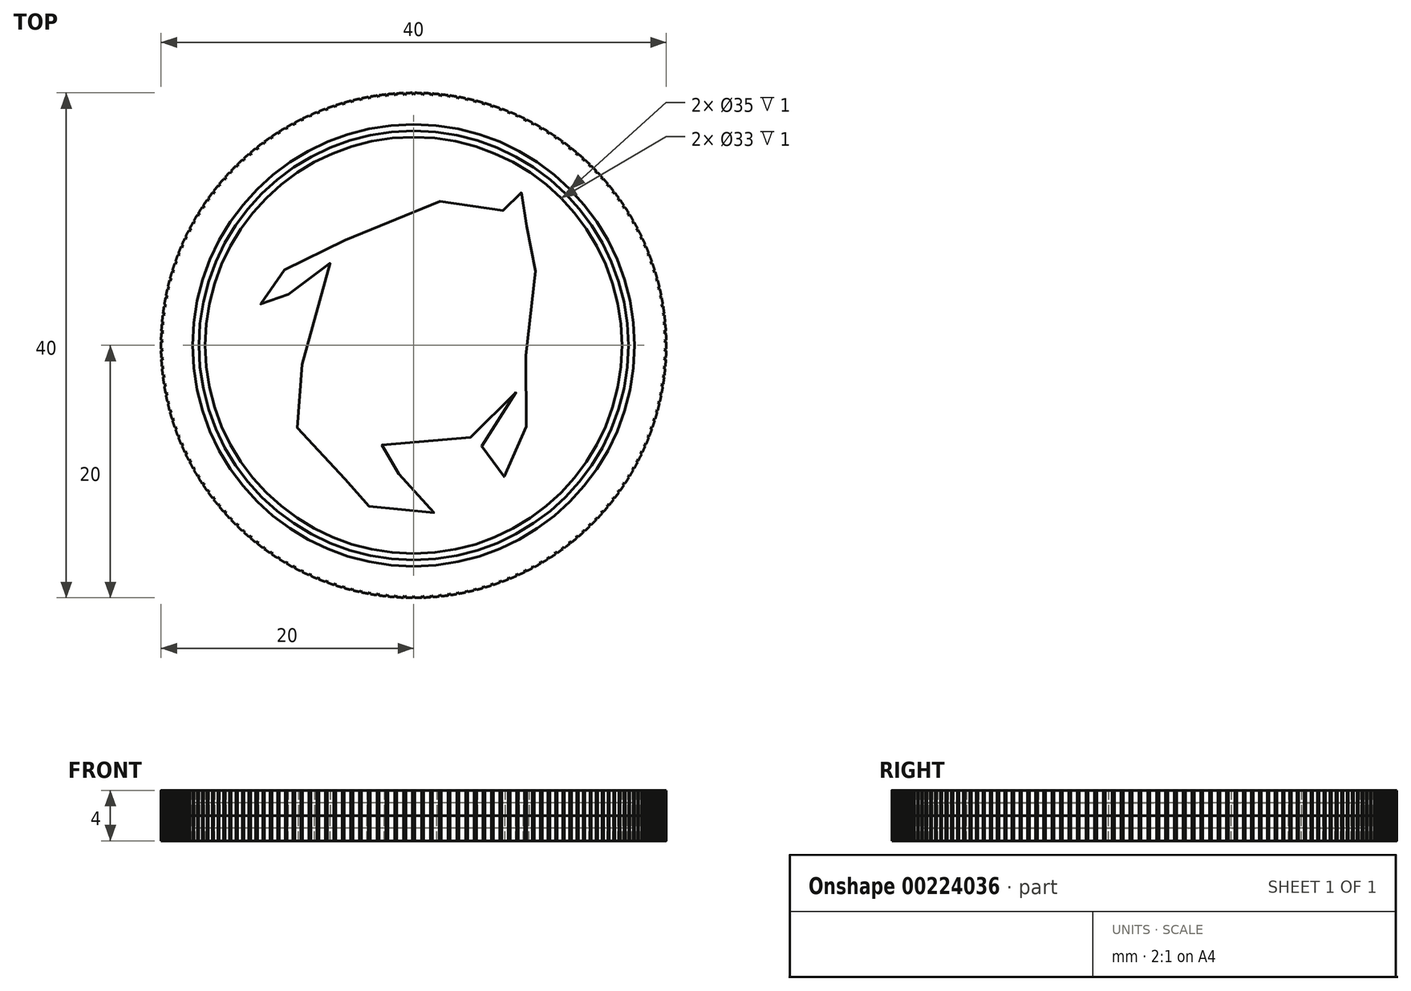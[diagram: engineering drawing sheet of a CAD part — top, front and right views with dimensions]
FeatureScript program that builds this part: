
annotation { "Feature Type Name" : "Feature", "Feature Type Description" : "" }
export const myFeature = defineFeature(function(context is Context, id is Id, definition is map)
    precondition{}
    {
        {
            var Q0;
            Q0=qCreatedBy(makeId("Top.planeOp"),FACE);
            var sketch = newSketch(context, id + "F0", { "sketchPlane" : qUnion([Q0])});
            skCircle(sketch, "E0", {"center": v(0, 0) * mm, "radius": 20 * mm});
            skCircle(sketch, "E1", {"center": v(0, 0) * mm, "radius": 17.5 * mm});
            skCircle(sketch, "E2", {"center": v(0, 0) * mm, "radius": 17 * mm});
            skCircle(sketch, "E3", {"center": v(0, 0) * mm, "radius": 16.5 * mm});
            skLineSegment(sketch, "E4", {"start": v(0, 19.85) * mm, "end": v(0.09, 20) * mm});
            skLineSegment(sketch, "E5", {"start": v(0, 19.85) * mm, "end": v(-0.09, 20) * mm});
            skPoint(sketch, "E6.center", {"position": v(0.03, 0) * mm});
            skLineSegment(sketch, "E7.1.0", {"start": v(0.7, 19.84) * mm, "end": v(0.8, 19.98) * mm});
            skLineSegment(sketch, "E7.1.1", {"start": v(0.7, 19.84) * mm, "end": v(0.62, 20) * mm});
            skLineSegment(sketch, "E7.2.0", {"start": v(1.4, 19.8) * mm, "end": v(1.5, 19.94) * mm});
            skLineSegment(sketch, "E7.2.1", {"start": v(1.4, 19.8) * mm, "end": v(1.32, 19.96) * mm});
            skLineSegment(sketch, "E7.3.0", {"start": v(2.1, 19.74) * mm, "end": v(2.2, 19.88) * mm});
            skLineSegment(sketch, "E7.3.1", {"start": v(2.1, 19.74) * mm, "end": v(2.03, 19.9) * mm});
            skLineSegment(sketch, "E7.4.0", {"start": v(2.8, 19.65) * mm, "end": v(2.9, 19.79) * mm});
            skLineSegment(sketch, "E7.4.1", {"start": v(2.8, 19.65) * mm, "end": v(2.73, 19.81) * mm});
            skLineSegment(sketch, "E7.5.0", {"start": v(3.49, 19.54) * mm, "end": v(3.6, 19.67) * mm});
            skLineSegment(sketch, "E7.5.1", {"start": v(3.49, 19.54) * mm, "end": v(3.43, 19.7) * mm});
            skLineSegment(sketch, "E7.6.0", {"start": v(4.17, 19.4) * mm, "end": v(4.29, 19.53) * mm});
            skLineSegment(sketch, "E7.6.1", {"start": v(4.17, 19.4) * mm, "end": v(4.12, 19.57) * mm});
            skLineSegment(sketch, "E7.7.0", {"start": v(4.86, 19.25) * mm, "end": v(4.98, 19.37) * mm});
            skLineSegment(sketch, "E7.7.1", {"start": v(4.86, 19.25) * mm, "end": v(4.8, 19.41) * mm});
            skLineSegment(sketch, "E7.8.0", {"start": v(5.53, 19.06) * mm, "end": v(5.66, 19.18) * mm});
            skLineSegment(sketch, "E7.8.1", {"start": v(5.53, 19.06) * mm, "end": v(5.49, 19.23) * mm});
            skLineSegment(sketch, "E7.9.0", {"start": v(6.2, 18.86) * mm, "end": v(6.33, 18.97) * mm});
            skLineSegment(sketch, "E7.9.1", {"start": v(6.2, 18.86) * mm, "end": v(6.17, 19.03) * mm});
            skLineSegment(sketch, "E7.10.0", {"start": v(6.86, 18.63) * mm, "end": v(7, 18.74) * mm});
            skLineSegment(sketch, "E7.10.1", {"start": v(6.86, 18.63) * mm, "end": v(6.83, 18.8) * mm});
            skLineSegment(sketch, "E7.11.0", {"start": v(7.52, 18.37) * mm, "end": v(7.65, 18.48) * mm});
            skLineSegment(sketch, "E7.11.1", {"start": v(7.52, 18.37) * mm, "end": v(7.5, 18.54) * mm});
            skLineSegment(sketch, "E7.12.0", {"start": v(8.16, 18.1) * mm, "end": v(8.3, 18.2) * mm});
            skLineSegment(sketch, "E7.12.1", {"start": v(8.16, 18.1) * mm, "end": v(8.14, 18.27) * mm});
            skLineSegment(sketch, "E7.13.0", {"start": v(8.8, 17.8) * mm, "end": v(8.94, 17.9) * mm});
            skLineSegment(sketch, "E7.13.1", {"start": v(8.8, 17.8) * mm, "end": v(8.78, 17.97) * mm});
            skLineSegment(sketch, "E7.14.0", {"start": v(9.42, 17.48) * mm, "end": v(9.56, 17.57) * mm});
            skLineSegment(sketch, "E7.14.1", {"start": v(9.42, 17.48) * mm, "end": v(9.41, 17.65) * mm});
            skLineSegment(sketch, "E7.15.0", {"start": v(10.03, 17.13) * mm, "end": v(10.18, 17.22) * mm});
            skLineSegment(sketch, "E7.15.1", {"start": v(10.03, 17.13) * mm, "end": v(10.03, 17.3) * mm});
            skLineSegment(sketch, "E7.16.0", {"start": v(10.62, 16.77) * mm, "end": v(10.78, 16.85) * mm});
            skLineSegment(sketch, "E7.16.1", {"start": v(10.62, 16.77) * mm, "end": v(10.63, 16.94) * mm});
            skLineSegment(sketch, "E7.17.0", {"start": v(11.2, 16.38) * mm, "end": v(11.37, 16.46) * mm});
            skLineSegment(sketch, "E7.17.1", {"start": v(11.2, 16.38) * mm, "end": v(11.22, 16.55) * mm});
            skLineSegment(sketch, "E7.18.0", {"start": v(11.78, 15.98) * mm, "end": v(11.94, 16.05) * mm});
            skLineSegment(sketch, "E7.18.1", {"start": v(11.78, 15.98) * mm, "end": v(11.8, 16.15) * mm});
            skLineSegment(sketch, "E7.19.0", {"start": v(12.34, 15.55) * mm, "end": v(12.5, 15.61) * mm});
            skLineSegment(sketch, "E7.19.1", {"start": v(12.34, 15.55) * mm, "end": v(12.36, 15.72) * mm});
            skLineSegment(sketch, "E7.20.0", {"start": v(12.88, 15.1) * mm, "end": v(13.04, 15.16) * mm});
            skLineSegment(sketch, "E7.20.1", {"start": v(12.88, 15.1) * mm, "end": v(12.9, 15.28) * mm});
            skLineSegment(sketch, "E7.21.0", {"start": v(13.4, 14.64) * mm, "end": v(13.57, 14.7) * mm});
            skLineSegment(sketch, "E7.21.1", {"start": v(13.4, 14.64) * mm, "end": v(13.44, 14.81) * mm});
            skLineSegment(sketch, "E7.22.0", {"start": v(13.91, 14.16) * mm, "end": v(14.08, 14.2) * mm});
            skLineSegment(sketch, "E7.22.1", {"start": v(13.91, 14.16) * mm, "end": v(13.95, 14.33) * mm});
            skLineSegment(sketch, "E7.23.0", {"start": v(14.4, 13.66) * mm, "end": v(14.57, 13.7) * mm});
            skLineSegment(sketch, "E7.23.1", {"start": v(14.4, 13.66) * mm, "end": v(14.45, 13.83) * mm});
            skLineSegment(sketch, "E7.24.0", {"start": v(14.88, 13.14) * mm, "end": v(15.05, 13.18) * mm});
            skLineSegment(sketch, "E7.24.1", {"start": v(14.88, 13.14) * mm, "end": v(14.93, 13.3) * mm});
            skLineSegment(sketch, "E7.25.0", {"start": v(15.33, 12.6) * mm, "end": v(15.5, 12.64) * mm});
            skLineSegment(sketch, "E7.25.1", {"start": v(15.33, 12.6) * mm, "end": v(15.4, 12.77) * mm});
            skLineSegment(sketch, "E7.26.0", {"start": v(15.77, 12.06) * mm, "end": v(15.94, 12.08) * mm});
            skLineSegment(sketch, "E7.26.1", {"start": v(15.77, 12.06) * mm, "end": v(15.83, 12.22) * mm});
            skLineSegment(sketch, "E7.27.0", {"start": v(16.18, 11.5) * mm, "end": v(16.35, 11.51) * mm});
            skLineSegment(sketch, "E7.27.1", {"start": v(16.18, 11.5) * mm, "end": v(16.25, 11.65) * mm});
            skLineSegment(sketch, "E7.28.0", {"start": v(16.58, 10.92) * mm, "end": v(16.75, 10.93) * mm});
            skLineSegment(sketch, "E7.28.1", {"start": v(16.58, 10.92) * mm, "end": v(16.65, 11.07) * mm});
            skLineSegment(sketch, "E7.29.0", {"start": v(16.95, 10.33) * mm, "end": v(17.13, 10.33) * mm});
            skLineSegment(sketch, "E7.29.1", {"start": v(16.95, 10.33) * mm, "end": v(17.04, 10.48) * mm});
            skLineSegment(sketch, "E7.30.0", {"start": v(17.3, 9.72) * mm, "end": v(17.48, 9.72) * mm});
            skLineSegment(sketch, "E7.30.1", {"start": v(17.3, 9.72) * mm, "end": v(17.4, 9.87) * mm});
            skLineSegment(sketch, "E7.31.0", {"start": v(17.64, 9.1) * mm, "end": v(17.81, 9.1) * mm});
            skLineSegment(sketch, "E7.31.1", {"start": v(17.64, 9.1) * mm, "end": v(17.73, 9.25) * mm});
            skLineSegment(sketch, "E7.32.0", {"start": v(17.95, 8.48) * mm, "end": v(18.12, 8.46) * mm});
            skLineSegment(sketch, "E7.32.1", {"start": v(17.95, 8.48) * mm, "end": v(18.05, 8.62) * mm});
            skLineSegment(sketch, "E7.33.0", {"start": v(18.24, 7.84) * mm, "end": v(18.4, 7.82) * mm});
            skLineSegment(sketch, "E7.33.1", {"start": v(18.24, 7.84) * mm, "end": v(18.34, 7.98) * mm});
            skLineSegment(sketch, "E7.34.0", {"start": v(18.5, 7.19) * mm, "end": v(18.67, 7.16) * mm});
            skLineSegment(sketch, "E7.34.1", {"start": v(18.5, 7.19) * mm, "end": v(18.61, 7.32) * mm});
            skLineSegment(sketch, "E7.35.0", {"start": v(18.74, 6.53) * mm, "end": v(18.91, 6.5) * mm});
            skLineSegment(sketch, "E7.35.1", {"start": v(18.74, 6.53) * mm, "end": v(18.86, 6.66) * mm});
            skLineSegment(sketch, "E7.36.0", {"start": v(18.96, 5.87) * mm, "end": v(19.13, 5.83) * mm});
            skLineSegment(sketch, "E7.36.1", {"start": v(18.96, 5.87) * mm, "end": v(19.08, 6) * mm});
            skLineSegment(sketch, "E7.37.0", {"start": v(19.16, 5.2) * mm, "end": v(19.33, 5.15) * mm});
            skLineSegment(sketch, "E7.37.1", {"start": v(19.16, 5.2) * mm, "end": v(19.28, 5.32) * mm});
            skLineSegment(sketch, "E7.38.0", {"start": v(19.33, 4.51) * mm, "end": v(19.5, 4.46) * mm});
            skLineSegment(sketch, "E7.38.1", {"start": v(19.33, 4.51) * mm, "end": v(19.46, 4.63) * mm});
            skLineSegment(sketch, "E7.39.0", {"start": v(19.48, 3.83) * mm, "end": v(19.64, 3.77) * mm});
            skLineSegment(sketch, "E7.39.1", {"start": v(19.48, 3.83) * mm, "end": v(19.6, 3.94) * mm});
            skLineSegment(sketch, "E7.40.0", {"start": v(19.6, 3.14) * mm, "end": v(19.76, 3.08) * mm});
            skLineSegment(sketch, "E7.40.1", {"start": v(19.6, 3.14) * mm, "end": v(19.73, 3.25) * mm});
            skLineSegment(sketch, "E7.41.0", {"start": v(19.7, 2.45) * mm, "end": v(19.86, 2.38) * mm});
            skLineSegment(sketch, "E7.41.1", {"start": v(19.7, 2.45) * mm, "end": v(19.84, 2.55) * mm});
            skLineSegment(sketch, "E7.42.0", {"start": v(19.77, 1.75) * mm, "end": v(19.93, 1.68) * mm});
            skLineSegment(sketch, "E7.42.1", {"start": v(19.77, 1.75) * mm, "end": v(19.91, 1.85) * mm});
            skLineSegment(sketch, "E7.43.0", {"start": v(19.82, 1.05) * mm, "end": v(19.98, 0.97) * mm});
            skLineSegment(sketch, "E7.43.1", {"start": v(19.82, 1.05) * mm, "end": v(19.97, 1.14) * mm});
            skLineSegment(sketch, "E7.44.0", {"start": v(19.85, 0.35) * mm, "end": v(20, 0.27) * mm});
            skLineSegment(sketch, "E7.44.1", {"start": v(19.85, 0.35) * mm, "end": v(20, 0.44) * mm});
            skLineSegment(sketch, "E7.45.0", {"start": v(19.85, -0.35) * mm, "end": v(20, -0.44) * mm});
            skLineSegment(sketch, "E7.45.1", {"start": v(19.85, -0.35) * mm, "end": v(20, -0.27) * mm});
            skLineSegment(sketch, "E7.46.0", {"start": v(19.82, -1.05) * mm, "end": v(19.97, -1.14) * mm});
            skLineSegment(sketch, "E7.46.1", {"start": v(19.82, -1.05) * mm, "end": v(19.98, -0.97) * mm});
            skLineSegment(sketch, "E7.47.0", {"start": v(19.77, -1.75) * mm, "end": v(19.91, -1.85) * mm});
            skLineSegment(sketch, "E7.47.1", {"start": v(19.77, -1.75) * mm, "end": v(19.93, -1.68) * mm});
            skLineSegment(sketch, "E7.48.0", {"start": v(19.7, -2.45) * mm, "end": v(19.84, -2.55) * mm});
            skLineSegment(sketch, "E7.48.1", {"start": v(19.7, -2.45) * mm, "end": v(19.86, -2.38) * mm});
            skLineSegment(sketch, "E7.49.0", {"start": v(19.6, -3.14) * mm, "end": v(19.73, -3.25) * mm});
            skLineSegment(sketch, "E7.49.1", {"start": v(19.6, -3.14) * mm, "end": v(19.76, -3.08) * mm});
            skLineSegment(sketch, "E7.50.0", {"start": v(19.48, -3.83) * mm, "end": v(19.6, -3.94) * mm});
            skLineSegment(sketch, "E7.50.1", {"start": v(19.48, -3.83) * mm, "end": v(19.64, -3.77) * mm});
            skLineSegment(sketch, "E7.51.0", {"start": v(19.33, -4.51) * mm, "end": v(19.46, -4.63) * mm});
            skLineSegment(sketch, "E7.51.1", {"start": v(19.33, -4.51) * mm, "end": v(19.5, -4.46) * mm});
            skLineSegment(sketch, "E7.52.0", {"start": v(19.16, -5.2) * mm, "end": v(19.28, -5.32) * mm});
            skLineSegment(sketch, "E7.52.1", {"start": v(19.16, -5.2) * mm, "end": v(19.33, -5.15) * mm});
            skLineSegment(sketch, "E7.53.0", {"start": v(18.96, -5.87) * mm, "end": v(19.08, -6) * mm});
            skLineSegment(sketch, "E7.53.1", {"start": v(18.96, -5.87) * mm, "end": v(19.13, -5.83) * mm});
            skLineSegment(sketch, "E7.54.0", {"start": v(18.74, -6.53) * mm, "end": v(18.86, -6.66) * mm});
            skLineSegment(sketch, "E7.54.1", {"start": v(18.74, -6.53) * mm, "end": v(18.91, -6.5) * mm});
            skLineSegment(sketch, "E7.55.0", {"start": v(18.5, -7.19) * mm, "end": v(18.61, -7.32) * mm});
            skLineSegment(sketch, "E7.55.1", {"start": v(18.5, -7.19) * mm, "end": v(18.67, -7.16) * mm});
            skLineSegment(sketch, "E7.56.0", {"start": v(18.24, -7.84) * mm, "end": v(18.34, -7.98) * mm});
            skLineSegment(sketch, "E7.56.1", {"start": v(18.24, -7.84) * mm, "end": v(18.4, -7.82) * mm});
            skLineSegment(sketch, "E7.57.0", {"start": v(17.95, -8.48) * mm, "end": v(18.05, -8.62) * mm});
            skLineSegment(sketch, "E7.57.1", {"start": v(17.95, -8.48) * mm, "end": v(18.12, -8.46) * mm});
            skLineSegment(sketch, "E7.58.0", {"start": v(17.64, -9.1) * mm, "end": v(17.73, -9.25) * mm});
            skLineSegment(sketch, "E7.58.1", {"start": v(17.64, -9.1) * mm, "end": v(17.81, -9.1) * mm});
            skLineSegment(sketch, "E7.59.0", {"start": v(17.3, -9.72) * mm, "end": v(17.4, -9.87) * mm});
            skLineSegment(sketch, "E7.59.1", {"start": v(17.3, -9.72) * mm, "end": v(17.48, -9.72) * mm});
            skLineSegment(sketch, "E7.60.0", {"start": v(16.95, -10.33) * mm, "end": v(17.04, -10.48) * mm});
            skLineSegment(sketch, "E7.60.1", {"start": v(16.95, -10.33) * mm, "end": v(17.13, -10.33) * mm});
            skLineSegment(sketch, "E7.61.0", {"start": v(16.58, -10.92) * mm, "end": v(16.65, -11.07) * mm});
            skLineSegment(sketch, "E7.61.1", {"start": v(16.58, -10.92) * mm, "end": v(16.75, -10.93) * mm});
            skLineSegment(sketch, "E7.62.0", {"start": v(16.18, -11.5) * mm, "end": v(16.25, -11.65) * mm});
            skLineSegment(sketch, "E7.62.1", {"start": v(16.18, -11.5) * mm, "end": v(16.35, -11.51) * mm});
            skLineSegment(sketch, "E7.63.0", {"start": v(15.77, -12.06) * mm, "end": v(15.83, -12.22) * mm});
            skLineSegment(sketch, "E7.63.1", {"start": v(15.77, -12.06) * mm, "end": v(15.94, -12.08) * mm});
            skLineSegment(sketch, "E7.64.0", {"start": v(15.33, -12.6) * mm, "end": v(15.4, -12.77) * mm});
            skLineSegment(sketch, "E7.64.1", {"start": v(15.33, -12.6) * mm, "end": v(15.5, -12.64) * mm});
            skLineSegment(sketch, "E7.65.0", {"start": v(14.88, -13.14) * mm, "end": v(14.93, -13.3) * mm});
            skLineSegment(sketch, "E7.65.1", {"start": v(14.88, -13.14) * mm, "end": v(15.05, -13.18) * mm});
            skLineSegment(sketch, "E7.66.0", {"start": v(14.4, -13.66) * mm, "end": v(14.45, -13.83) * mm});
            skLineSegment(sketch, "E7.66.1", {"start": v(14.4, -13.66) * mm, "end": v(14.57, -13.7) * mm});
            skLineSegment(sketch, "E7.67.0", {"start": v(13.91, -14.16) * mm, "end": v(13.95, -14.33) * mm});
            skLineSegment(sketch, "E7.67.1", {"start": v(13.91, -14.16) * mm, "end": v(14.08, -14.2) * mm});
            skLineSegment(sketch, "E7.68.0", {"start": v(13.4, -14.64) * mm, "end": v(13.44, -14.81) * mm});
            skLineSegment(sketch, "E7.68.1", {"start": v(13.4, -14.64) * mm, "end": v(13.57, -14.7) * mm});
            skLineSegment(sketch, "E7.69.0", {"start": v(12.88, -15.1) * mm, "end": v(12.9, -15.28) * mm});
            skLineSegment(sketch, "E7.69.1", {"start": v(12.88, -15.1) * mm, "end": v(13.04, -15.16) * mm});
            skLineSegment(sketch, "E7.70.0", {"start": v(12.34, -15.55) * mm, "end": v(12.36, -15.72) * mm});
            skLineSegment(sketch, "E7.70.1", {"start": v(12.34, -15.55) * mm, "end": v(12.5, -15.61) * mm});
            skLineSegment(sketch, "E7.71.0", {"start": v(11.78, -15.98) * mm, "end": v(11.8, -16.15) * mm});
            skLineSegment(sketch, "E7.71.1", {"start": v(11.78, -15.98) * mm, "end": v(11.94, -16.05) * mm});
            skLineSegment(sketch, "E7.72.0", {"start": v(11.2, -16.38) * mm, "end": v(11.22, -16.55) * mm});
            skLineSegment(sketch, "E7.72.1", {"start": v(11.2, -16.38) * mm, "end": v(11.37, -16.46) * mm});
            skLineSegment(sketch, "E7.73.0", {"start": v(10.62, -16.77) * mm, "end": v(10.63, -16.94) * mm});
            skLineSegment(sketch, "E7.73.1", {"start": v(10.62, -16.77) * mm, "end": v(10.78, -16.85) * mm});
            skLineSegment(sketch, "E7.74.0", {"start": v(10.03, -17.13) * mm, "end": v(10.03, -17.3) * mm});
            skLineSegment(sketch, "E7.74.1", {"start": v(10.03, -17.13) * mm, "end": v(10.18, -17.22) * mm});
            skLineSegment(sketch, "E7.75.0", {"start": v(9.42, -17.48) * mm, "end": v(9.41, -17.65) * mm});
            skLineSegment(sketch, "E7.75.1", {"start": v(9.42, -17.48) * mm, "end": v(9.56, -17.57) * mm});
            skLineSegment(sketch, "E7.76.0", {"start": v(8.8, -17.8) * mm, "end": v(8.78, -17.97) * mm});
            skLineSegment(sketch, "E7.76.1", {"start": v(8.8, -17.8) * mm, "end": v(8.94, -17.9) * mm});
            skLineSegment(sketch, "E7.77.0", {"start": v(8.16, -18.1) * mm, "end": v(8.14, -18.27) * mm});
            skLineSegment(sketch, "E7.77.1", {"start": v(8.16, -18.1) * mm, "end": v(8.3, -18.2) * mm});
            skLineSegment(sketch, "E7.78.0", {"start": v(7.52, -18.37) * mm, "end": v(7.5, -18.54) * mm});
            skLineSegment(sketch, "E7.78.1", {"start": v(7.52, -18.37) * mm, "end": v(7.65, -18.48) * mm});
            skLineSegment(sketch, "E7.79.0", {"start": v(6.86, -18.63) * mm, "end": v(6.83, -18.8) * mm});
            skLineSegment(sketch, "E7.79.1", {"start": v(6.86, -18.63) * mm, "end": v(7, -18.74) * mm});
            skLineSegment(sketch, "E7.80.0", {"start": v(6.2, -18.86) * mm, "end": v(6.17, -19.03) * mm});
            skLineSegment(sketch, "E7.80.1", {"start": v(6.2, -18.86) * mm, "end": v(6.33, -18.97) * mm});
            skLineSegment(sketch, "E7.81.0", {"start": v(5.53, -19.06) * mm, "end": v(5.49, -19.23) * mm});
            skLineSegment(sketch, "E7.81.1", {"start": v(5.53, -19.06) * mm, "end": v(5.66, -19.18) * mm});
            skLineSegment(sketch, "E7.82.0", {"start": v(4.86, -19.25) * mm, "end": v(4.8, -19.41) * mm});
            skLineSegment(sketch, "E7.82.1", {"start": v(4.86, -19.25) * mm, "end": v(4.98, -19.37) * mm});
            skLineSegment(sketch, "E7.83.0", {"start": v(4.17, -19.4) * mm, "end": v(4.12, -19.57) * mm});
            skLineSegment(sketch, "E7.83.1", {"start": v(4.17, -19.4) * mm, "end": v(4.29, -19.53) * mm});
            skLineSegment(sketch, "E7.84.0", {"start": v(3.49, -19.54) * mm, "end": v(3.43, -19.7) * mm});
            skLineSegment(sketch, "E7.84.1", {"start": v(3.49, -19.54) * mm, "end": v(3.6, -19.67) * mm});
            skLineSegment(sketch, "E7.85.0", {"start": v(2.8, -19.65) * mm, "end": v(2.73, -19.81) * mm});
            skLineSegment(sketch, "E7.85.1", {"start": v(2.8, -19.65) * mm, "end": v(2.9, -19.79) * mm});
            skLineSegment(sketch, "E7.86.0", {"start": v(2.1, -19.74) * mm, "end": v(2.03, -19.9) * mm});
            skLineSegment(sketch, "E7.86.1", {"start": v(2.1, -19.74) * mm, "end": v(2.2, -19.88) * mm});
            skLineSegment(sketch, "E7.87.0", {"start": v(1.4, -19.8) * mm, "end": v(1.32, -19.96) * mm});
            skLineSegment(sketch, "E7.87.1", {"start": v(1.4, -19.8) * mm, "end": v(1.5, -19.94) * mm});
            skLineSegment(sketch, "E7.88.0", {"start": v(0.7, -19.84) * mm, "end": v(0.62, -20) * mm});
            skLineSegment(sketch, "E7.88.1", {"start": v(0.7, -19.84) * mm, "end": v(0.8, -19.98) * mm});
            skLineSegment(sketch, "E7.89.0", {"start": v(0, -19.85) * mm, "end": v(-0.09, -20) * mm});
            skLineSegment(sketch, "E7.89.1", {"start": v(0, -19.85) * mm, "end": v(0.09, -20) * mm});
            skLineSegment(sketch, "E7.anchor1", {"start": v(0, 0) * mm, "end": v(0, 19.85) * mm, "construction": true});
            skLineSegment(sketch, "E7.anchor2", {"start": v(0, 0) * mm, "end": v(0, -19.85) * mm, "construction": true});
            skLineSegment(sketch, "E8.1.0", {"start": v(-0.7, -19.84) * mm, "end": v(-0.8, -19.98) * mm});
            skLineSegment(sketch, "E8.1.1", {"start": v(-0.7, -19.84) * mm, "end": v(-0.62, -20) * mm});
            skLineSegment(sketch, "E8.2.0", {"start": v(-1.4, -19.8) * mm, "end": v(-1.5, -19.94) * mm});
            skLineSegment(sketch, "E8.2.1", {"start": v(-1.4, -19.8) * mm, "end": v(-1.32, -19.96) * mm});
            skLineSegment(sketch, "E8.anchor1", {"start": v(0, 0) * mm, "end": v(-0.09, -20) * mm, "construction": true});
            skLineSegment(sketch, "E8.anchor2", {"start": v(0, 0) * mm, "end": v(0.09, 20) * mm, "construction": true});
            skLineSegment(sketch, "E9.2.3.0", {"start": v(-2.1, -19.74) * mm, "end": v(-2.2, -19.88) * mm});
            skLineSegment(sketch, "E9.3.3.0", {"start": v(-2.1, -19.74) * mm, "end": v(-2.03, -19.9) * mm});
            skLineSegment(sketch, "E9.2.4.0", {"start": v(-2.8, -19.65) * mm, "end": v(-2.9, -19.79) * mm});
            skLineSegment(sketch, "E9.3.4.0", {"start": v(-2.8, -19.65) * mm, "end": v(-2.73, -19.81) * mm});
            skLineSegment(sketch, "E9.2.5.0", {"start": v(-3.49, -19.54) * mm, "end": v(-3.6, -19.67) * mm});
            skLineSegment(sketch, "E9.3.5.0", {"start": v(-3.49, -19.54) * mm, "end": v(-3.43, -19.7) * mm});
            skLineSegment(sketch, "E9.2.6.0", {"start": v(-4.17, -19.4) * mm, "end": v(-4.29, -19.53) * mm});
            skLineSegment(sketch, "E9.3.6.0", {"start": v(-4.17, -19.4) * mm, "end": v(-4.12, -19.57) * mm});
            skLineSegment(sketch, "E9.2.7.0", {"start": v(-4.86, -19.25) * mm, "end": v(-4.98, -19.37) * mm});
            skLineSegment(sketch, "E9.3.7.0", {"start": v(-4.86, -19.25) * mm, "end": v(-4.8, -19.41) * mm});
            skLineSegment(sketch, "E9.2.8.0", {"start": v(-5.53, -19.06) * mm, "end": v(-5.66, -19.18) * mm});
            skLineSegment(sketch, "E9.3.8.0", {"start": v(-5.53, -19.06) * mm, "end": v(-5.49, -19.23) * mm});
            skLineSegment(sketch, "E9.2.9.0", {"start": v(-6.2, -18.86) * mm, "end": v(-6.33, -18.97) * mm});
            skLineSegment(sketch, "E9.3.9.0", {"start": v(-6.2, -18.86) * mm, "end": v(-6.17, -19.03) * mm});
            skLineSegment(sketch, "E9.2.10.0", {"start": v(-6.86, -18.63) * mm, "end": v(-7, -18.74) * mm});
            skLineSegment(sketch, "E9.3.10.0", {"start": v(-6.86, -18.63) * mm, "end": v(-6.83, -18.8) * mm});
            skLineSegment(sketch, "E9.2.11.0", {"start": v(-7.52, -18.37) * mm, "end": v(-7.65, -18.48) * mm});
            skLineSegment(sketch, "E9.3.11.0", {"start": v(-7.52, -18.37) * mm, "end": v(-7.5, -18.54) * mm});
            skLineSegment(sketch, "E9.2.12.0", {"start": v(-8.16, -18.1) * mm, "end": v(-8.3, -18.2) * mm});
            skLineSegment(sketch, "E9.3.12.0", {"start": v(-8.16, -18.1) * mm, "end": v(-8.14, -18.27) * mm});
            skLineSegment(sketch, "E9.2.13.0", {"start": v(-8.8, -17.8) * mm, "end": v(-8.94, -17.9) * mm});
            skLineSegment(sketch, "E9.3.13.0", {"start": v(-8.8, -17.8) * mm, "end": v(-8.78, -17.97) * mm});
            skLineSegment(sketch, "E9.2.14.0", {"start": v(-9.42, -17.48) * mm, "end": v(-9.56, -17.57) * mm});
            skLineSegment(sketch, "E9.3.14.0", {"start": v(-9.42, -17.48) * mm, "end": v(-9.41, -17.65) * mm});
            skLineSegment(sketch, "E9.2.15.0", {"start": v(-10.03, -17.13) * mm, "end": v(-10.18, -17.22) * mm});
            skLineSegment(sketch, "E9.3.15.0", {"start": v(-10.03, -17.13) * mm, "end": v(-10.03, -17.3) * mm});
            skLineSegment(sketch, "E9.2.16.0", {"start": v(-10.62, -16.77) * mm, "end": v(-10.78, -16.85) * mm});
            skLineSegment(sketch, "E9.3.16.0", {"start": v(-10.62, -16.77) * mm, "end": v(-10.63, -16.94) * mm});
            skLineSegment(sketch, "E9.2.17.0", {"start": v(-11.2, -16.38) * mm, "end": v(-11.37, -16.46) * mm});
            skLineSegment(sketch, "E9.3.17.0", {"start": v(-11.2, -16.38) * mm, "end": v(-11.22, -16.55) * mm});
            skLineSegment(sketch, "E9.2.18.0", {"start": v(-11.78, -15.98) * mm, "end": v(-11.94, -16.05) * mm});
            skLineSegment(sketch, "E9.3.18.0", {"start": v(-11.78, -15.98) * mm, "end": v(-11.8, -16.15) * mm});
            skLineSegment(sketch, "E9.2.19.0", {"start": v(-12.34, -15.55) * mm, "end": v(-12.5, -15.61) * mm});
            skLineSegment(sketch, "E9.3.19.0", {"start": v(-12.34, -15.55) * mm, "end": v(-12.36, -15.72) * mm});
            skLineSegment(sketch, "E9.2.20.0", {"start": v(-12.88, -15.1) * mm, "end": v(-13.04, -15.16) * mm});
            skLineSegment(sketch, "E9.3.20.0", {"start": v(-12.88, -15.1) * mm, "end": v(-12.9, -15.28) * mm});
            skLineSegment(sketch, "E9.2.21.0", {"start": v(-13.4, -14.64) * mm, "end": v(-13.57, -14.7) * mm});
            skLineSegment(sketch, "E9.3.21.0", {"start": v(-13.4, -14.64) * mm, "end": v(-13.44, -14.81) * mm});
            skLineSegment(sketch, "E9.2.22.0", {"start": v(-13.91, -14.16) * mm, "end": v(-14.08, -14.2) * mm});
            skLineSegment(sketch, "E9.3.22.0", {"start": v(-13.91, -14.16) * mm, "end": v(-13.95, -14.33) * mm});
            skLineSegment(sketch, "E9.2.23.0", {"start": v(-14.4, -13.66) * mm, "end": v(-14.57, -13.7) * mm});
            skLineSegment(sketch, "E9.3.23.0", {"start": v(-14.4, -13.66) * mm, "end": v(-14.45, -13.83) * mm});
            skLineSegment(sketch, "E9.2.24.0", {"start": v(-14.88, -13.14) * mm, "end": v(-15.05, -13.18) * mm});
            skLineSegment(sketch, "E9.3.24.0", {"start": v(-14.88, -13.14) * mm, "end": v(-14.93, -13.3) * mm});
            skLineSegment(sketch, "E9.2.25.0", {"start": v(-15.33, -12.6) * mm, "end": v(-15.5, -12.64) * mm});
            skLineSegment(sketch, "E9.3.25.0", {"start": v(-15.33, -12.6) * mm, "end": v(-15.4, -12.77) * mm});
            skLineSegment(sketch, "E9.2.26.0", {"start": v(-15.77, -12.06) * mm, "end": v(-15.94, -12.08) * mm});
            skLineSegment(sketch, "E9.3.26.0", {"start": v(-15.77, -12.06) * mm, "end": v(-15.83, -12.22) * mm});
            skLineSegment(sketch, "E9.2.27.0", {"start": v(-16.18, -11.5) * mm, "end": v(-16.35, -11.51) * mm});
            skLineSegment(sketch, "E9.3.27.0", {"start": v(-16.18, -11.5) * mm, "end": v(-16.25, -11.65) * mm});
            skLineSegment(sketch, "E9.2.28.0", {"start": v(-16.58, -10.92) * mm, "end": v(-16.75, -10.93) * mm});
            skLineSegment(sketch, "E9.3.28.0", {"start": v(-16.58, -10.92) * mm, "end": v(-16.65, -11.07) * mm});
            skLineSegment(sketch, "E9.2.29.0", {"start": v(-16.95, -10.33) * mm, "end": v(-17.13, -10.33) * mm});
            skLineSegment(sketch, "E9.3.29.0", {"start": v(-16.95, -10.33) * mm, "end": v(-17.04, -10.48) * mm});
            skLineSegment(sketch, "E9.2.30.0", {"start": v(-17.3, -9.72) * mm, "end": v(-17.48, -9.72) * mm});
            skLineSegment(sketch, "E9.3.30.0", {"start": v(-17.3, -9.72) * mm, "end": v(-17.4, -9.87) * mm});
            skLineSegment(sketch, "E9.2.31.0", {"start": v(-17.64, -9.1) * mm, "end": v(-17.81, -9.1) * mm});
            skLineSegment(sketch, "E9.3.31.0", {"start": v(-17.64, -9.1) * mm, "end": v(-17.73, -9.25) * mm});
            skLineSegment(sketch, "E9.2.32.0", {"start": v(-17.95, -8.48) * mm, "end": v(-18.12, -8.46) * mm});
            skLineSegment(sketch, "E9.3.32.0", {"start": v(-17.95, -8.48) * mm, "end": v(-18.05, -8.62) * mm});
            skLineSegment(sketch, "E9.2.33.0", {"start": v(-18.24, -7.84) * mm, "end": v(-18.4, -7.82) * mm});
            skLineSegment(sketch, "E9.3.33.0", {"start": v(-18.24, -7.84) * mm, "end": v(-18.34, -7.98) * mm});
            skLineSegment(sketch, "E9.2.34.0", {"start": v(-18.5, -7.19) * mm, "end": v(-18.67, -7.16) * mm});
            skLineSegment(sketch, "E9.3.34.0", {"start": v(-18.5, -7.19) * mm, "end": v(-18.61, -7.32) * mm});
            skLineSegment(sketch, "E9.2.35.0", {"start": v(-18.74, -6.53) * mm, "end": v(-18.91, -6.5) * mm});
            skLineSegment(sketch, "E9.3.35.0", {"start": v(-18.74, -6.53) * mm, "end": v(-18.86, -6.66) * mm});
            skLineSegment(sketch, "E9.2.36.0", {"start": v(-18.96, -5.87) * mm, "end": v(-19.13, -5.83) * mm});
            skLineSegment(sketch, "E9.3.36.0", {"start": v(-18.96, -5.87) * mm, "end": v(-19.08, -6) * mm});
            skLineSegment(sketch, "E9.2.37.0", {"start": v(-19.16, -5.2) * mm, "end": v(-19.33, -5.15) * mm});
            skLineSegment(sketch, "E9.3.37.0", {"start": v(-19.16, -5.2) * mm, "end": v(-19.28, -5.32) * mm});
            skLineSegment(sketch, "E9.2.38.0", {"start": v(-19.33, -4.51) * mm, "end": v(-19.5, -4.46) * mm});
            skLineSegment(sketch, "E9.3.38.0", {"start": v(-19.33, -4.51) * mm, "end": v(-19.46, -4.63) * mm});
            skLineSegment(sketch, "E9.2.39.0", {"start": v(-19.48, -3.83) * mm, "end": v(-19.64, -3.77) * mm});
            skLineSegment(sketch, "E9.3.39.0", {"start": v(-19.48, -3.83) * mm, "end": v(-19.6, -3.94) * mm});
            skLineSegment(sketch, "E9.2.40.0", {"start": v(-19.6, -3.14) * mm, "end": v(-19.76, -3.08) * mm});
            skLineSegment(sketch, "E9.3.40.0", {"start": v(-19.6, -3.14) * mm, "end": v(-19.73, -3.25) * mm});
            skLineSegment(sketch, "E9.2.41.0", {"start": v(-19.7, -2.45) * mm, "end": v(-19.86, -2.38) * mm});
            skLineSegment(sketch, "E9.3.41.0", {"start": v(-19.7, -2.45) * mm, "end": v(-19.84, -2.55) * mm});
            skLineSegment(sketch, "E9.2.42.0", {"start": v(-19.77, -1.75) * mm, "end": v(-19.93, -1.68) * mm});
            skLineSegment(sketch, "E9.3.42.0", {"start": v(-19.77, -1.75) * mm, "end": v(-19.91, -1.85) * mm});
            skLineSegment(sketch, "E9.2.43.0", {"start": v(-19.82, -1.05) * mm, "end": v(-19.98, -0.97) * mm});
            skLineSegment(sketch, "E9.3.43.0", {"start": v(-19.82, -1.05) * mm, "end": v(-19.97, -1.14) * mm});
            skLineSegment(sketch, "E9.2.44.0", {"start": v(-19.85, -0.35) * mm, "end": v(-20, -0.27) * mm});
            skLineSegment(sketch, "E9.3.44.0", {"start": v(-19.85, -0.35) * mm, "end": v(-20, -0.44) * mm});
            skLineSegment(sketch, "E9.2.45.0", {"start": v(-19.85, 0.35) * mm, "end": v(-20, 0.44) * mm});
            skLineSegment(sketch, "E9.3.45.0", {"start": v(-19.85, 0.35) * mm, "end": v(-20, 0.27) * mm});
            skLineSegment(sketch, "E9.2.46.0", {"start": v(-19.82, 1.05) * mm, "end": v(-19.97, 1.14) * mm});
            skLineSegment(sketch, "E9.3.46.0", {"start": v(-19.82, 1.05) * mm, "end": v(-19.98, 0.97) * mm});
            skLineSegment(sketch, "E9.2.47.0", {"start": v(-19.77, 1.75) * mm, "end": v(-19.91, 1.85) * mm});
            skLineSegment(sketch, "E9.3.47.0", {"start": v(-19.77, 1.75) * mm, "end": v(-19.93, 1.68) * mm});
            skLineSegment(sketch, "E9.2.48.0", {"start": v(-19.7, 2.45) * mm, "end": v(-19.84, 2.55) * mm});
            skLineSegment(sketch, "E9.3.48.0", {"start": v(-19.7, 2.45) * mm, "end": v(-19.86, 2.38) * mm});
            skLineSegment(sketch, "E9.2.49.0", {"start": v(-19.6, 3.14) * mm, "end": v(-19.73, 3.25) * mm});
            skLineSegment(sketch, "E9.3.49.0", {"start": v(-19.6, 3.14) * mm, "end": v(-19.76, 3.08) * mm});
            skLineSegment(sketch, "E9.2.50.0", {"start": v(-19.48, 3.83) * mm, "end": v(-19.6, 3.94) * mm});
            skLineSegment(sketch, "E9.3.50.0", {"start": v(-19.48, 3.83) * mm, "end": v(-19.64, 3.77) * mm});
            skLineSegment(sketch, "E9.2.51.0", {"start": v(-19.33, 4.51) * mm, "end": v(-19.46, 4.63) * mm});
            skLineSegment(sketch, "E9.3.51.0", {"start": v(-19.33, 4.51) * mm, "end": v(-19.5, 4.46) * mm});
            skLineSegment(sketch, "E9.2.52.0", {"start": v(-19.16, 5.2) * mm, "end": v(-19.28, 5.32) * mm});
            skLineSegment(sketch, "E9.3.52.0", {"start": v(-19.16, 5.2) * mm, "end": v(-19.33, 5.15) * mm});
            skLineSegment(sketch, "E9.2.53.0", {"start": v(-18.96, 5.87) * mm, "end": v(-19.08, 6) * mm});
            skLineSegment(sketch, "E9.3.53.0", {"start": v(-18.96, 5.87) * mm, "end": v(-19.13, 5.83) * mm});
            skLineSegment(sketch, "E9.2.54.0", {"start": v(-18.74, 6.53) * mm, "end": v(-18.86, 6.66) * mm});
            skLineSegment(sketch, "E9.3.54.0", {"start": v(-18.74, 6.53) * mm, "end": v(-18.91, 6.5) * mm});
            skLineSegment(sketch, "E9.2.55.0", {"start": v(-18.5, 7.19) * mm, "end": v(-18.61, 7.32) * mm});
            skLineSegment(sketch, "E9.3.55.0", {"start": v(-18.5, 7.19) * mm, "end": v(-18.67, 7.16) * mm});
            skLineSegment(sketch, "E9.2.56.0", {"start": v(-18.24, 7.84) * mm, "end": v(-18.34, 7.98) * mm});
            skLineSegment(sketch, "E9.3.56.0", {"start": v(-18.24, 7.84) * mm, "end": v(-18.4, 7.82) * mm});
            skLineSegment(sketch, "E9.2.57.0", {"start": v(-17.95, 8.48) * mm, "end": v(-18.05, 8.62) * mm});
            skLineSegment(sketch, "E9.3.57.0", {"start": v(-17.95, 8.48) * mm, "end": v(-18.12, 8.46) * mm});
            skLineSegment(sketch, "E9.2.58.0", {"start": v(-17.64, 9.1) * mm, "end": v(-17.73, 9.25) * mm});
            skLineSegment(sketch, "E9.3.58.0", {"start": v(-17.64, 9.1) * mm, "end": v(-17.81, 9.1) * mm});
            skLineSegment(sketch, "E9.2.59.0", {"start": v(-17.3, 9.72) * mm, "end": v(-17.4, 9.87) * mm});
            skLineSegment(sketch, "E9.3.59.0", {"start": v(-17.3, 9.72) * mm, "end": v(-17.48, 9.72) * mm});
            skLineSegment(sketch, "E9.2.60.0", {"start": v(-16.95, 10.33) * mm, "end": v(-17.04, 10.48) * mm});
            skLineSegment(sketch, "E9.3.60.0", {"start": v(-16.95, 10.33) * mm, "end": v(-17.13, 10.33) * mm});
            skLineSegment(sketch, "E9.2.61.0", {"start": v(-16.58, 10.92) * mm, "end": v(-16.65, 11.07) * mm});
            skLineSegment(sketch, "E9.3.61.0", {"start": v(-16.58, 10.92) * mm, "end": v(-16.75, 10.93) * mm});
            skLineSegment(sketch, "E9.2.62.0", {"start": v(-16.18, 11.5) * mm, "end": v(-16.25, 11.65) * mm});
            skLineSegment(sketch, "E9.3.62.0", {"start": v(-16.18, 11.5) * mm, "end": v(-16.35, 11.51) * mm});
            skLineSegment(sketch, "E9.2.63.0", {"start": v(-15.77, 12.06) * mm, "end": v(-15.83, 12.22) * mm});
            skLineSegment(sketch, "E9.3.63.0", {"start": v(-15.77, 12.06) * mm, "end": v(-15.94, 12.08) * mm});
            skLineSegment(sketch, "E9.2.64.0", {"start": v(-15.33, 12.6) * mm, "end": v(-15.4, 12.77) * mm});
            skLineSegment(sketch, "E9.3.64.0", {"start": v(-15.33, 12.6) * mm, "end": v(-15.5, 12.64) * mm});
            skLineSegment(sketch, "E9.2.65.0", {"start": v(-14.88, 13.14) * mm, "end": v(-14.93, 13.3) * mm});
            skLineSegment(sketch, "E9.3.65.0", {"start": v(-14.88, 13.14) * mm, "end": v(-15.05, 13.18) * mm});
            skLineSegment(sketch, "E9.2.66.0", {"start": v(-14.4, 13.66) * mm, "end": v(-14.45, 13.83) * mm});
            skLineSegment(sketch, "E9.3.66.0", {"start": v(-14.4, 13.66) * mm, "end": v(-14.57, 13.7) * mm});
            skLineSegment(sketch, "E9.2.67.0", {"start": v(-13.91, 14.16) * mm, "end": v(-13.95, 14.33) * mm});
            skLineSegment(sketch, "E9.3.67.0", {"start": v(-13.91, 14.16) * mm, "end": v(-14.08, 14.2) * mm});
            skLineSegment(sketch, "E9.2.68.0", {"start": v(-13.4, 14.64) * mm, "end": v(-13.44, 14.81) * mm});
            skLineSegment(sketch, "E9.3.68.0", {"start": v(-13.4, 14.64) * mm, "end": v(-13.57, 14.7) * mm});
            skLineSegment(sketch, "E9.2.69.0", {"start": v(-12.88, 15.1) * mm, "end": v(-12.9, 15.28) * mm});
            skLineSegment(sketch, "E9.3.69.0", {"start": v(-12.88, 15.1) * mm, "end": v(-13.04, 15.16) * mm});
            skLineSegment(sketch, "E9.2.70.0", {"start": v(-12.34, 15.55) * mm, "end": v(-12.36, 15.72) * mm});
            skLineSegment(sketch, "E9.3.70.0", {"start": v(-12.34, 15.55) * mm, "end": v(-12.5, 15.61) * mm});
            skLineSegment(sketch, "E9.2.71.0", {"start": v(-11.78, 15.98) * mm, "end": v(-11.8, 16.15) * mm});
            skLineSegment(sketch, "E9.3.71.0", {"start": v(-11.78, 15.98) * mm, "end": v(-11.94, 16.05) * mm});
            skLineSegment(sketch, "E9.2.72.0", {"start": v(-11.2, 16.38) * mm, "end": v(-11.22, 16.55) * mm});
            skLineSegment(sketch, "E9.3.72.0", {"start": v(-11.2, 16.38) * mm, "end": v(-11.37, 16.46) * mm});
            skLineSegment(sketch, "E9.2.73.0", {"start": v(-10.62, 16.77) * mm, "end": v(-10.63, 16.94) * mm});
            skLineSegment(sketch, "E9.3.73.0", {"start": v(-10.62, 16.77) * mm, "end": v(-10.78, 16.85) * mm});
            skLineSegment(sketch, "E9.2.74.0", {"start": v(-10.03, 17.13) * mm, "end": v(-10.03, 17.3) * mm});
            skLineSegment(sketch, "E9.3.74.0", {"start": v(-10.03, 17.13) * mm, "end": v(-10.18, 17.22) * mm});
            skLineSegment(sketch, "E9.2.75.0", {"start": v(-9.42, 17.48) * mm, "end": v(-9.41, 17.65) * mm});
            skLineSegment(sketch, "E9.3.75.0", {"start": v(-9.42, 17.48) * mm, "end": v(-9.56, 17.57) * mm});
            skLineSegment(sketch, "E9.2.76.0", {"start": v(-8.8, 17.8) * mm, "end": v(-8.78, 17.97) * mm});
            skLineSegment(sketch, "E9.3.76.0", {"start": v(-8.8, 17.8) * mm, "end": v(-8.94, 17.9) * mm});
            skLineSegment(sketch, "E9.2.77.0", {"start": v(-8.16, 18.1) * mm, "end": v(-8.14, 18.27) * mm});
            skLineSegment(sketch, "E9.3.77.0", {"start": v(-8.16, 18.1) * mm, "end": v(-8.3, 18.2) * mm});
            skLineSegment(sketch, "E9.2.78.0", {"start": v(-7.52, 18.37) * mm, "end": v(-7.5, 18.54) * mm});
            skLineSegment(sketch, "E9.3.78.0", {"start": v(-7.52, 18.37) * mm, "end": v(-7.65, 18.48) * mm});
            skLineSegment(sketch, "E9.2.79.0", {"start": v(-6.86, 18.63) * mm, "end": v(-6.83, 18.8) * mm});
            skLineSegment(sketch, "E9.3.79.0", {"start": v(-6.86, 18.63) * mm, "end": v(-7, 18.74) * mm});
            skLineSegment(sketch, "E9.2.80.0", {"start": v(-6.2, 18.86) * mm, "end": v(-6.17, 19.03) * mm});
            skLineSegment(sketch, "E9.3.80.0", {"start": v(-6.2, 18.86) * mm, "end": v(-6.33, 18.97) * mm});
            skLineSegment(sketch, "E9.2.81.0", {"start": v(-5.53, 19.06) * mm, "end": v(-5.49, 19.23) * mm});
            skLineSegment(sketch, "E9.3.81.0", {"start": v(-5.53, 19.06) * mm, "end": v(-5.66, 19.18) * mm});
            skLineSegment(sketch, "E9.2.82.0", {"start": v(-4.86, 19.25) * mm, "end": v(-4.8, 19.41) * mm});
            skLineSegment(sketch, "E9.3.82.0", {"start": v(-4.86, 19.25) * mm, "end": v(-4.98, 19.37) * mm});
            skLineSegment(sketch, "E9.2.83.0", {"start": v(-4.17, 19.4) * mm, "end": v(-4.12, 19.57) * mm});
            skLineSegment(sketch, "E9.3.83.0", {"start": v(-4.17, 19.4) * mm, "end": v(-4.29, 19.53) * mm});
            skLineSegment(sketch, "E9.2.84.0", {"start": v(-3.49, 19.54) * mm, "end": v(-3.43, 19.7) * mm});
            skLineSegment(sketch, "E9.3.84.0", {"start": v(-3.49, 19.54) * mm, "end": v(-3.6, 19.67) * mm});
            skLineSegment(sketch, "E9.2.85.0", {"start": v(-2.8, 19.65) * mm, "end": v(-2.73, 19.81) * mm});
            skLineSegment(sketch, "E9.3.85.0", {"start": v(-2.8, 19.65) * mm, "end": v(-2.9, 19.79) * mm});
            skLineSegment(sketch, "E9.2.86.0", {"start": v(-2.1, 19.74) * mm, "end": v(-2.03, 19.9) * mm});
            skLineSegment(sketch, "E9.3.86.0", {"start": v(-2.1, 19.74) * mm, "end": v(-2.2, 19.88) * mm});
            skLineSegment(sketch, "E9.2.87.0", {"start": v(-1.4, 19.8) * mm, "end": v(-1.32, 19.96) * mm});
            skLineSegment(sketch, "E9.3.87.0", {"start": v(-1.4, 19.8) * mm, "end": v(-1.5, 19.94) * mm});
            skLineSegment(sketch, "E9.2.88.0", {"start": v(-0.7, 19.84) * mm, "end": v(-0.62, 20) * mm});
            skLineSegment(sketch, "E9.3.88.0", {"start": v(-0.7, 19.84) * mm, "end": v(-0.8, 19.98) * mm});
            skSolve(sketch);
        }
        {
            var Q0;
            Q0=qCreatedBy(makeId("Top.planeOp"),FACE);
            var sketch = newSketch(context, id + "F1", { "sketchPlane" : qUnion([Q0])});
            skFitSpline(sketch, "E10", {"points": [v(-5.43, 8.34) * mm, v(-1.12, 11.02) * mm, v(4.7, 10.97) * mm, v(6.23, 10.4) * mm, v(7.01, 10.6) * mm, v(7.12, 11.44) * mm, v(6.28, 12.12) * mm, v(7.49, 12.39) * mm, v(10.11, 11.18) * mm, v(9.11, 10.92) * mm, v(8.9, 9.5) * mm, v(10.22, 8.03) * mm, v(9.48, 6.72) * mm, v(9.7, 5.77) * mm, v(10.06, 2.3) * mm, v(8.7, -1.37) * mm, v(8.8, -1.9) * mm, v(9.06, -5.88) * mm, v(8.27, -8.35) * mm, v(8.27, -9.5) * mm, v(6.9, -10.4) * mm, v(5.86, -9.4) * mm, v(5.23, -9.09) * mm, v(5.18, -8.14) * mm, v(6.9, -7.67) * mm, v(8.01, -5.36) * mm, v(7.9, -2.84) * mm, v(5.75, -6.15) * mm, v(0.98, -8.4) * mm, v(-2.6, -7.88) * mm, v(-3.54, -8.3) * mm, v(-2.7, -9.56) * mm, v(-0.8, -10.24) * mm, v(1.24, -11.03) * mm, v(1.82, -12.76) * mm, v(0, -14.07) * mm, v(-3.7, -12.97) * mm, v(-2.9, -12.55) * mm, v(-2.33, -12.18) * mm, v(-2.9, -11.55) * mm, v(-8.37, -9.4) * mm, v(-9.58, -7.67) * mm, v(-8.47, -5.3) * mm, v(-7.84, -3.89) * mm, v(-9.1, 0) * mm, v(-6.69, 6.24) * mm, v(-6.69, 6.82) * mm, v(-7.27, 6.77) * mm, v(-9.94, 4.4) * mm, v(-9.52, 3.2) * mm, v(-10.68, 2.41) * mm, v(-11.89, 2.99) * mm, v(-12.25, 3.88) * mm, v(-11.41, 4.46) * mm, v(-10.84, 5.14) * mm, v(-9.63, 6.5) * mm, v(-6.64, 7.77) * mm, v(-5.43, 8.34) * mm]});
            skSolve(sketch);
        }
        {
            var Q0;
            Q0=makeQuery(id+"F0.imprint","IMPRINT",FACE,{"disambiguationData":[TD([[makeQuery(id+"F0.imprint","IMPRINT",EDGE,{"derivedFrom":sQuery(id+"F0.wireOp",EDGE,"E3")}),1.0]])]});
            var Q1;
            Q1=makeQuery(id+"F0.imprint","IMPRINT",FACE,{"disambiguationData":[TD([[makeQuery(id+"F0.imprint","IMPRINT",EDGE,{"derivedFrom":sQuery(id+"F0.wireOp",EDGE,"E2")}),1.0]])]});
            var Q2;
            Q2=makeQuery(id+"F0.imprint","IMPRINT",FACE,{"disambiguationData":[TD([[makeQuery(id+"F0.imprint","IMPRINT",EDGE,{"derivedFrom":sQuery(id+"F0.wireOp",EDGE,"E1")}),1.0]])]});
            var Q3;
            Q3=makeQuery(id+"F0.imprint","IMPRINT",FACE,{"disambiguationData":[TD([[makeQuery(id+"F0.imprint","IMPRINT",EDGE,{"derivedFrom":sQuery(id+"F0.wireOp",EDGE,"E1")}),-1.0]])]});
            extrude(context, id + "F2", {"entities" : qUnion([Q0, Q1, Q2, Q3]), "depth" : 1 * mm});
        }
        {
            var Q0;
            Q0=makeQuery(id+"F0.imprint","IMPRINT",FACE,{"disambiguationData":[TD([[makeQuery(id+"F0.imprint","IMPRINT",EDGE,{"derivedFrom":sQuery(id+"F0.wireOp",EDGE,"E1")}),-1.0]])]});
            var Q1;
            Q1=makeQuery(id+"F0.imprint","IMPRINT",FACE,{"disambiguationData":[TD([[makeQuery(id+"F0.imprint","IMPRINT",EDGE,{"derivedFrom":sQuery(id+"F0.wireOp",EDGE,"E2")}),1.0]])]});
            extrude(context, id + "F3", {"entities" : qUnion([Q0, Q1]), "operationType" : NewBodyOperationType.ADD, "depth" : 2 * mm});
        }
        {
            var Q0;
            Q0=makeQuery(id+"F1.imprint","IMPRINT",FACE,{"disambiguationData":[TD([[makeQuery(id+"F1.imprint","IMPRINT",EDGE,{"derivedFrom":sQuery(id+"F1.wireOp",EDGE,"E10")}),-1.0]])]});
            var Q1;
            Q1=sQuery(id+"F1.wireOp",EDGE,"E10");
            extrude(context, id + "F4", {"entities" : qUnion([Q0]), "surfaceEntities" : qUnion([Q1]), "depth" : 2 * mm});
        }
        {
            var Q0;
            Q0=makeQuery(id+"F4.opExtrude","SWEPT_BODY",BODY,{"disambiguationData":[OSD([sQuery(id+"F1.wireOp",EDGE,"E10")])]});
            var Q1;
            Q1=makeQuery(id+"F2.opExtrude","SWEPT_BODY",BODY,{"disambiguationData":[OSD([sQuery(id+"F0.wireOp",EDGE,"E0"),sQuery(id+"F0.wireOp",EDGE,"E7.1.0"),sQuery(id+"F0.wireOp",EDGE,"E7.1.1"),sQuery(id+"F0.wireOp",EDGE,"E7.2.0"),sQuery(id+"F0.wireOp",EDGE,"E7.2.1"),sQuery(id+"F0.wireOp",EDGE,"E7.3.0"),sQuery(id+"F0.wireOp",EDGE,"E7.3.1"),sQuery(id+"F0.wireOp",EDGE,"E7.4.0"),sQuery(id+"F0.wireOp",EDGE,"E7.4.1"),sQuery(id+"F0.wireOp",EDGE,"E7.5.0"),sQuery(id+"F0.wireOp",EDGE,"E7.5.1"),sQuery(id+"F0.wireOp",EDGE,"E7.6.0"),sQuery(id+"F0.wireOp",EDGE,"E7.6.1"),sQuery(id+"F0.wireOp",EDGE,"E7.7.0"),sQuery(id+"F0.wireOp",EDGE,"E7.7.1"),sQuery(id+"F0.wireOp",EDGE,"E7.8.0"),sQuery(id+"F0.wireOp",EDGE,"E7.8.1"),sQuery(id+"F0.wireOp",EDGE,"E7.9.0"),sQuery(id+"F0.wireOp",EDGE,"E7.9.1"),sQuery(id+"F0.wireOp",EDGE,"E7.10.0"),sQuery(id+"F0.wireOp",EDGE,"E7.10.1"),sQuery(id+"F0.wireOp",EDGE,"E7.11.0"),sQuery(id+"F0.wireOp",EDGE,"E7.11.1"),sQuery(id+"F0.wireOp",EDGE,"E7.12.0"),sQuery(id+"F0.wireOp",EDGE,"E7.12.1"),sQuery(id+"F0.wireOp",EDGE,"E7.13.0"),sQuery(id+"F0.wireOp",EDGE,"E7.13.1"),sQuery(id+"F0.wireOp",EDGE,"E7.14.0"),sQuery(id+"F0.wireOp",EDGE,"E7.14.1"),sQuery(id+"F0.wireOp",EDGE,"E7.15.0"),sQuery(id+"F0.wireOp",EDGE,"E7.15.1"),sQuery(id+"F0.wireOp",EDGE,"E7.16.0"),sQuery(id+"F0.wireOp",EDGE,"E7.16.1"),sQuery(id+"F0.wireOp",EDGE,"E7.17.0"),sQuery(id+"F0.wireOp",EDGE,"E7.17.1"),sQuery(id+"F0.wireOp",EDGE,"E7.18.0"),sQuery(id+"F0.wireOp",EDGE,"E7.18.1"),sQuery(id+"F0.wireOp",EDGE,"E7.19.0"),sQuery(id+"F0.wireOp",EDGE,"E7.19.1"),sQuery(id+"F0.wireOp",EDGE,"E7.20.0"),sQuery(id+"F0.wireOp",EDGE,"E7.20.1"),sQuery(id+"F0.wireOp",EDGE,"E7.21.0"),sQuery(id+"F0.wireOp",EDGE,"E7.21.1"),sQuery(id+"F0.wireOp",EDGE,"E7.22.0"),sQuery(id+"F0.wireOp",EDGE,"E7.22.1"),sQuery(id+"F0.wireOp",EDGE,"E7.23.0"),sQuery(id+"F0.wireOp",EDGE,"E7.23.1"),sQuery(id+"F0.wireOp",EDGE,"E7.24.0"),sQuery(id+"F0.wireOp",EDGE,"E7.24.1"),sQuery(id+"F0.wireOp",EDGE,"E7.25.0"),sQuery(id+"F0.wireOp",EDGE,"E7.25.1"),sQuery(id+"F0.wireOp",EDGE,"E7.26.0"),sQuery(id+"F0.wireOp",EDGE,"E7.26.1"),sQuery(id+"F0.wireOp",EDGE,"E7.27.0"),sQuery(id+"F0.wireOp",EDGE,"E7.27.1"),sQuery(id+"F0.wireOp",EDGE,"E7.28.0"),sQuery(id+"F0.wireOp",EDGE,"E7.28.1"),sQuery(id+"F0.wireOp",EDGE,"E7.29.0"),sQuery(id+"F0.wireOp",EDGE,"E7.29.1"),sQuery(id+"F0.wireOp",EDGE,"E7.30.0"),sQuery(id+"F0.wireOp",EDGE,"E7.30.1"),sQuery(id+"F0.wireOp",EDGE,"E7.31.0"),sQuery(id+"F0.wireOp",EDGE,"E7.31.1"),sQuery(id+"F0.wireOp",EDGE,"E7.32.0"),sQuery(id+"F0.wireOp",EDGE,"E7.32.1"),sQuery(id+"F0.wireOp",EDGE,"E7.33.0"),sQuery(id+"F0.wireOp",EDGE,"E7.33.1"),sQuery(id+"F0.wireOp",EDGE,"E7.34.0"),sQuery(id+"F0.wireOp",EDGE,"E7.34.1"),sQuery(id+"F0.wireOp",EDGE,"E7.35.0"),sQuery(id+"F0.wireOp",EDGE,"E7.35.1"),sQuery(id+"F0.wireOp",EDGE,"E7.36.0"),sQuery(id+"F0.wireOp",EDGE,"E7.36.1"),sQuery(id+"F0.wireOp",EDGE,"E7.37.0"),sQuery(id+"F0.wireOp",EDGE,"E7.37.1"),sQuery(id+"F0.wireOp",EDGE,"E7.38.0"),sQuery(id+"F0.wireOp",EDGE,"E7.38.1"),sQuery(id+"F0.wireOp",EDGE,"E7.39.0"),sQuery(id+"F0.wireOp",EDGE,"E7.39.1"),sQuery(id+"F0.wireOp",EDGE,"E7.40.0"),sQuery(id+"F0.wireOp",EDGE,"E7.40.1"),sQuery(id+"F0.wireOp",EDGE,"E7.41.0"),sQuery(id+"F0.wireOp",EDGE,"E7.41.1"),sQuery(id+"F0.wireOp",EDGE,"E7.42.0"),sQuery(id+"F0.wireOp",EDGE,"E7.42.1"),sQuery(id+"F0.wireOp",EDGE,"E7.43.0"),sQuery(id+"F0.wireOp",EDGE,"E7.43.1"),sQuery(id+"F0.wireOp",EDGE,"E7.44.0"),sQuery(id+"F0.wireOp",EDGE,"E7.44.1"),sQuery(id+"F0.wireOp",EDGE,"E7.45.0"),sQuery(id+"F0.wireOp",EDGE,"E7.45.1"),sQuery(id+"F0.wireOp",EDGE,"E7.46.0"),sQuery(id+"F0.wireOp",EDGE,"E7.46.1"),sQuery(id+"F0.wireOp",EDGE,"E7.47.0"),sQuery(id+"F0.wireOp",EDGE,"E7.47.1"),sQuery(id+"F0.wireOp",EDGE,"E7.48.0"),sQuery(id+"F0.wireOp",EDGE,"E7.48.1"),sQuery(id+"F0.wireOp",EDGE,"E7.49.0"),sQuery(id+"F0.wireOp",EDGE,"E7.49.1"),sQuery(id+"F0.wireOp",EDGE,"E7.50.0"),sQuery(id+"F0.wireOp",EDGE,"E7.50.1"),sQuery(id+"F0.wireOp",EDGE,"E7.51.0"),sQuery(id+"F0.wireOp",EDGE,"E7.51.1"),sQuery(id+"F0.wireOp",EDGE,"E7.52.0"),sQuery(id+"F0.wireOp",EDGE,"E7.52.1"),sQuery(id+"F0.wireOp",EDGE,"E7.53.0"),sQuery(id+"F0.wireOp",EDGE,"E7.53.1"),sQuery(id+"F0.wireOp",EDGE,"E7.54.0"),sQuery(id+"F0.wireOp",EDGE,"E7.54.1"),sQuery(id+"F0.wireOp",EDGE,"E7.55.0"),sQuery(id+"F0.wireOp",EDGE,"E7.55.1"),sQuery(id+"F0.wireOp",EDGE,"E7.56.0"),sQuery(id+"F0.wireOp",EDGE,"E7.56.1"),sQuery(id+"F0.wireOp",EDGE,"E7.57.0"),sQuery(id+"F0.wireOp",EDGE,"E7.57.1"),sQuery(id+"F0.wireOp",EDGE,"E7.58.0"),sQuery(id+"F0.wireOp",EDGE,"E7.58.1"),sQuery(id+"F0.wireOp",EDGE,"E7.59.0"),sQuery(id+"F0.wireOp",EDGE,"E7.59.1"),sQuery(id+"F0.wireOp",EDGE,"E7.60.0"),sQuery(id+"F0.wireOp",EDGE,"E7.60.1"),sQuery(id+"F0.wireOp",EDGE,"E7.61.0"),sQuery(id+"F0.wireOp",EDGE,"E7.61.1"),sQuery(id+"F0.wireOp",EDGE,"E7.62.0"),sQuery(id+"F0.wireOp",EDGE,"E7.62.1"),sQuery(id+"F0.wireOp",EDGE,"E7.63.0"),sQuery(id+"F0.wireOp",EDGE,"E7.63.1"),sQuery(id+"F0.wireOp",EDGE,"E7.64.0"),sQuery(id+"F0.wireOp",EDGE,"E7.64.1"),sQuery(id+"F0.wireOp",EDGE,"E7.65.0"),sQuery(id+"F0.wireOp",EDGE,"E7.65.1"),sQuery(id+"F0.wireOp",EDGE,"E7.66.0"),sQuery(id+"F0.wireOp",EDGE,"E7.66.1"),sQuery(id+"F0.wireOp",EDGE,"E7.67.0"),sQuery(id+"F0.wireOp",EDGE,"E7.67.1"),sQuery(id+"F0.wireOp",EDGE,"E7.68.0"),sQuery(id+"F0.wireOp",EDGE,"E7.68.1"),sQuery(id+"F0.wireOp",EDGE,"E7.69.0"),sQuery(id+"F0.wireOp",EDGE,"E7.69.1"),sQuery(id+"F0.wireOp",EDGE,"E7.70.0"),sQuery(id+"F0.wireOp",EDGE,"E7.70.1"),sQuery(id+"F0.wireOp",EDGE,"E7.71.0"),sQuery(id+"F0.wireOp",EDGE,"E7.71.1"),sQuery(id+"F0.wireOp",EDGE,"E7.72.0"),sQuery(id+"F0.wireOp",EDGE,"E7.72.1"),sQuery(id+"F0.wireOp",EDGE,"E7.73.0"),sQuery(id+"F0.wireOp",EDGE,"E7.73.1"),sQuery(id+"F0.wireOp",EDGE,"E7.74.0"),sQuery(id+"F0.wireOp",EDGE,"E7.74.1"),sQuery(id+"F0.wireOp",EDGE,"E7.75.0"),sQuery(id+"F0.wireOp",EDGE,"E7.75.1"),sQuery(id+"F0.wireOp",EDGE,"E7.76.0"),sQuery(id+"F0.wireOp",EDGE,"E7.76.1"),sQuery(id+"F0.wireOp",EDGE,"E7.77.0"),sQuery(id+"F0.wireOp",EDGE,"E7.77.1"),sQuery(id+"F0.wireOp",EDGE,"E7.78.0"),sQuery(id+"F0.wireOp",EDGE,"E7.78.1"),sQuery(id+"F0.wireOp",EDGE,"E7.79.0"),sQuery(id+"F0.wireOp",EDGE,"E7.79.1"),sQuery(id+"F0.wireOp",EDGE,"E7.80.0"),sQuery(id+"F0.wireOp",EDGE,"E7.80.1"),sQuery(id+"F0.wireOp",EDGE,"E7.81.0"),sQuery(id+"F0.wireOp",EDGE,"E7.81.1"),sQuery(id+"F0.wireOp",EDGE,"E7.82.0"),sQuery(id+"F0.wireOp",EDGE,"E7.82.1"),sQuery(id+"F0.wireOp",EDGE,"E7.83.0"),sQuery(id+"F0.wireOp",EDGE,"E7.83.1"),sQuery(id+"F0.wireOp",EDGE,"E7.84.0"),sQuery(id+"F0.wireOp",EDGE,"E7.84.1"),sQuery(id+"F0.wireOp",EDGE,"E7.85.0"),sQuery(id+"F0.wireOp",EDGE,"E7.85.1"),sQuery(id+"F0.wireOp",EDGE,"E7.86.0"),sQuery(id+"F0.wireOp",EDGE,"E7.86.1"),sQuery(id+"F0.wireOp",EDGE,"E7.87.0"),sQuery(id+"F0.wireOp",EDGE,"E7.87.1"),sQuery(id+"F0.wireOp",EDGE,"E7.88.0"),sQuery(id+"F0.wireOp",EDGE,"E7.88.1"),sQuery(id+"F0.wireOp",EDGE,"E7.89.0"),sQuery(id+"F0.wireOp",EDGE,"E7.89.1"),sQuery(id+"F0.wireOp",EDGE,"E8.1.0"),sQuery(id+"F0.wireOp",EDGE,"E8.1.1"),sQuery(id+"F0.wireOp",EDGE,"E8.2.0"),sQuery(id+"F0.wireOp",EDGE,"E8.2.1"),sQuery(id+"F0.wireOp",EDGE,"E9.2.3.0"),sQuery(id+"F0.wireOp",EDGE,"E9.3.3.0"),sQuery(id+"F0.wireOp",EDGE,"E9.2.4.0"),sQuery(id+"F0.wireOp",EDGE,"E9.3.4.0"),sQuery(id+"F0.wireOp",EDGE,"E9.2.5.0"),sQuery(id+"F0.wireOp",EDGE,"E9.3.5.0"),sQuery(id+"F0.wireOp",EDGE,"E9.2.6.0"),sQuery(id+"F0.wireOp",EDGE,"E9.3.6.0"),sQuery(id+"F0.wireOp",EDGE,"E9.2.7.0"),sQuery(id+"F0.wireOp",EDGE,"E9.3.7.0"),sQuery(id+"F0.wireOp",EDGE,"E9.2.8.0"),sQuery(id+"F0.wireOp",EDGE,"E9.3.8.0"),sQuery(id+"F0.wireOp",EDGE,"E9.2.9.0"),sQuery(id+"F0.wireOp",EDGE,"E9.3.9.0"),sQuery(id+"F0.wireOp",EDGE,"E9.2.10.0"),sQuery(id+"F0.wireOp",EDGE,"E9.3.10.0"),sQuery(id+"F0.wireOp",EDGE,"E9.2.11.0"),sQuery(id+"F0.wireOp",EDGE,"E9.3.11.0"),sQuery(id+"F0.wireOp",EDGE,"E9.2.12.0"),sQuery(id+"F0.wireOp",EDGE,"E9.3.12.0"),sQuery(id+"F0.wireOp",EDGE,"E9.2.13.0"),sQuery(id+"F0.wireOp",EDGE,"E9.3.13.0"),sQuery(id+"F0.wireOp",EDGE,"E9.2.14.0"),sQuery(id+"F0.wireOp",EDGE,"E9.3.14.0"),sQuery(id+"F0.wireOp",EDGE,"E9.2.15.0"),sQuery(id+"F0.wireOp",EDGE,"E9.3.15.0"),sQuery(id+"F0.wireOp",EDGE,"E9.2.16.0"),sQuery(id+"F0.wireOp",EDGE,"E9.3.16.0"),sQuery(id+"F0.wireOp",EDGE,"E9.2.17.0"),sQuery(id+"F0.wireOp",EDGE,"E9.3.17.0"),sQuery(id+"F0.wireOp",EDGE,"E9.2.18.0"),sQuery(id+"F0.wireOp",EDGE,"E9.3.18.0"),sQuery(id+"F0.wireOp",EDGE,"E9.2.19.0"),sQuery(id+"F0.wireOp",EDGE,"E9.3.19.0"),sQuery(id+"F0.wireOp",EDGE,"E9.2.20.0"),sQuery(id+"F0.wireOp",EDGE,"E9.3.20.0"),sQuery(id+"F0.wireOp",EDGE,"E9.2.21.0"),sQuery(id+"F0.wireOp",EDGE,"E9.3.21.0"),sQuery(id+"F0.wireOp",EDGE,"E9.2.22.0"),sQuery(id+"F0.wireOp",EDGE,"E9.3.22.0"),sQuery(id+"F0.wireOp",EDGE,"E9.2.23.0"),sQuery(id+"F0.wireOp",EDGE,"E9.3.23.0"),sQuery(id+"F0.wireOp",EDGE,"E9.2.24.0"),sQuery(id+"F0.wireOp",EDGE,"E9.3.24.0"),sQuery(id+"F0.wireOp",EDGE,"E9.2.25.0"),sQuery(id+"F0.wireOp",EDGE,"E9.3.25.0"),sQuery(id+"F0.wireOp",EDGE,"E9.2.26.0"),sQuery(id+"F0.wireOp",EDGE,"E9.3.26.0"),sQuery(id+"F0.wireOp",EDGE,"E9.2.27.0"),sQuery(id+"F0.wireOp",EDGE,"E9.3.27.0"),sQuery(id+"F0.wireOp",EDGE,"E9.2.28.0"),sQuery(id+"F0.wireOp",EDGE,"E9.3.28.0"),sQuery(id+"F0.wireOp",EDGE,"E9.2.29.0"),sQuery(id+"F0.wireOp",EDGE,"E9.3.29.0"),sQuery(id+"F0.wireOp",EDGE,"E9.2.30.0"),sQuery(id+"F0.wireOp",EDGE,"E9.3.30.0"),sQuery(id+"F0.wireOp",EDGE,"E9.2.31.0"),sQuery(id+"F0.wireOp",EDGE,"E9.3.31.0"),sQuery(id+"F0.wireOp",EDGE,"E9.2.32.0"),sQuery(id+"F0.wireOp",EDGE,"E9.3.32.0"),sQuery(id+"F0.wireOp",EDGE,"E9.2.33.0"),sQuery(id+"F0.wireOp",EDGE,"E9.3.33.0"),sQuery(id+"F0.wireOp",EDGE,"E9.2.34.0"),sQuery(id+"F0.wireOp",EDGE,"E9.3.34.0"),sQuery(id+"F0.wireOp",EDGE,"E9.2.35.0"),sQuery(id+"F0.wireOp",EDGE,"E9.3.35.0"),sQuery(id+"F0.wireOp",EDGE,"E9.2.36.0"),sQuery(id+"F0.wireOp",EDGE,"E9.3.36.0"),sQuery(id+"F0.wireOp",EDGE,"E9.2.37.0"),sQuery(id+"F0.wireOp",EDGE,"E9.3.37.0"),sQuery(id+"F0.wireOp",EDGE,"E9.2.38.0"),sQuery(id+"F0.wireOp",EDGE,"E9.3.38.0"),sQuery(id+"F0.wireOp",EDGE,"E9.2.39.0"),sQuery(id+"F0.wireOp",EDGE,"E9.3.39.0"),sQuery(id+"F0.wireOp",EDGE,"E9.2.40.0"),sQuery(id+"F0.wireOp",EDGE,"E9.3.40.0"),sQuery(id+"F0.wireOp",EDGE,"E9.2.41.0"),sQuery(id+"F0.wireOp",EDGE,"E9.3.41.0"),sQuery(id+"F0.wireOp",EDGE,"E9.2.42.0"),sQuery(id+"F0.wireOp",EDGE,"E9.3.42.0"),sQuery(id+"F0.wireOp",EDGE,"E9.2.43.0"),sQuery(id+"F0.wireOp",EDGE,"E9.3.43.0"),sQuery(id+"F0.wireOp",EDGE,"E9.2.44.0"),sQuery(id+"F0.wireOp",EDGE,"E9.3.44.0"),sQuery(id+"F0.wireOp",EDGE,"E9.2.45.0"),sQuery(id+"F0.wireOp",EDGE,"E9.3.45.0"),sQuery(id+"F0.wireOp",EDGE,"E9.2.46.0"),sQuery(id+"F0.wireOp",EDGE,"E9.3.46.0"),sQuery(id+"F0.wireOp",EDGE,"E9.2.47.0"),sQuery(id+"F0.wireOp",EDGE,"E9.3.47.0"),sQuery(id+"F0.wireOp",EDGE,"E9.2.48.0"),sQuery(id+"F0.wireOp",EDGE,"E9.3.48.0"),sQuery(id+"F0.wireOp",EDGE,"E9.2.49.0"),sQuery(id+"F0.wireOp",EDGE,"E9.3.49.0"),sQuery(id+"F0.wireOp",EDGE,"E9.2.50.0"),sQuery(id+"F0.wireOp",EDGE,"E9.3.50.0"),sQuery(id+"F0.wireOp",EDGE,"E9.2.51.0"),sQuery(id+"F0.wireOp",EDGE,"E9.3.51.0"),sQuery(id+"F0.wireOp",EDGE,"E9.2.52.0"),sQuery(id+"F0.wireOp",EDGE,"E9.3.52.0"),sQuery(id+"F0.wireOp",EDGE,"E9.2.53.0"),sQuery(id+"F0.wireOp",EDGE,"E9.3.53.0"),sQuery(id+"F0.wireOp",EDGE,"E9.2.54.0"),sQuery(id+"F0.wireOp",EDGE,"E9.3.54.0"),sQuery(id+"F0.wireOp",EDGE,"E9.2.55.0"),sQuery(id+"F0.wireOp",EDGE,"E9.3.55.0"),sQuery(id+"F0.wireOp",EDGE,"E9.2.56.0"),sQuery(id+"F0.wireOp",EDGE,"E9.3.56.0"),sQuery(id+"F0.wireOp",EDGE,"E9.2.57.0"),sQuery(id+"F0.wireOp",EDGE,"E9.3.57.0"),sQuery(id+"F0.wireOp",EDGE,"E9.2.58.0"),sQuery(id+"F0.wireOp",EDGE,"E9.3.58.0"),sQuery(id+"F0.wireOp",EDGE,"E9.2.59.0"),sQuery(id+"F0.wireOp",EDGE,"E9.3.59.0"),sQuery(id+"F0.wireOp",EDGE,"E9.2.60.0"),sQuery(id+"F0.wireOp",EDGE,"E9.3.60.0"),sQuery(id+"F0.wireOp",EDGE,"E9.2.61.0"),sQuery(id+"F0.wireOp",EDGE,"E9.3.61.0"),sQuery(id+"F0.wireOp",EDGE,"E9.2.62.0"),sQuery(id+"F0.wireOp",EDGE,"E9.3.62.0"),sQuery(id+"F0.wireOp",EDGE,"E9.2.63.0"),sQuery(id+"F0.wireOp",EDGE,"E9.3.63.0"),sQuery(id+"F0.wireOp",EDGE,"E9.2.64.0"),sQuery(id+"F0.wireOp",EDGE,"E9.3.64.0"),sQuery(id+"F0.wireOp",EDGE,"E9.2.65.0"),sQuery(id+"F0.wireOp",EDGE,"E9.3.65.0"),sQuery(id+"F0.wireOp",EDGE,"E9.2.66.0"),sQuery(id+"F0.wireOp",EDGE,"E9.3.66.0"),sQuery(id+"F0.wireOp",EDGE,"E9.2.67.0"),sQuery(id+"F0.wireOp",EDGE,"E9.3.67.0"),sQuery(id+"F0.wireOp",EDGE,"E9.2.68.0"),sQuery(id+"F0.wireOp",EDGE,"E9.3.68.0"),sQuery(id+"F0.wireOp",EDGE,"E9.2.69.0"),sQuery(id+"F0.wireOp",EDGE,"E9.3.69.0"),sQuery(id+"F0.wireOp",EDGE,"E9.2.70.0"),sQuery(id+"F0.wireOp",EDGE,"E9.3.70.0"),sQuery(id+"F0.wireOp",EDGE,"E9.2.71.0"),sQuery(id+"F0.wireOp",EDGE,"E9.3.71.0"),sQuery(id+"F0.wireOp",EDGE,"E9.2.72.0"),sQuery(id+"F0.wireOp",EDGE,"E9.3.72.0"),sQuery(id+"F0.wireOp",EDGE,"E9.2.73.0"),sQuery(id+"F0.wireOp",EDGE,"E9.3.73.0"),sQuery(id+"F0.wireOp",EDGE,"E9.2.74.0"),sQuery(id+"F0.wireOp",EDGE,"E9.3.74.0"),sQuery(id+"F0.wireOp",EDGE,"E9.2.75.0"),sQuery(id+"F0.wireOp",EDGE,"E9.3.75.0"),sQuery(id+"F0.wireOp",EDGE,"E9.2.76.0"),sQuery(id+"F0.wireOp",EDGE,"E9.3.76.0"),sQuery(id+"F0.wireOp",EDGE,"E9.2.77.0"),sQuery(id+"F0.wireOp",EDGE,"E9.3.77.0"),sQuery(id+"F0.wireOp",EDGE,"E9.2.78.0"),sQuery(id+"F0.wireOp",EDGE,"E9.3.78.0"),sQuery(id+"F0.wireOp",EDGE,"E9.2.79.0"),sQuery(id+"F0.wireOp",EDGE,"E9.3.79.0"),sQuery(id+"F0.wireOp",EDGE,"E9.2.80.0"),sQuery(id+"F0.wireOp",EDGE,"E9.3.80.0"),sQuery(id+"F0.wireOp",EDGE,"E9.2.81.0"),sQuery(id+"F0.wireOp",EDGE,"E9.3.81.0"),sQuery(id+"F0.wireOp",EDGE,"E9.2.82.0"),sQuery(id+"F0.wireOp",EDGE,"E9.3.82.0"),sQuery(id+"F0.wireOp",EDGE,"E9.2.83.0"),sQuery(id+"F0.wireOp",EDGE,"E9.3.83.0"),sQuery(id+"F0.wireOp",EDGE,"E9.2.84.0"),sQuery(id+"F0.wireOp",EDGE,"E9.3.84.0"),sQuery(id+"F0.wireOp",EDGE,"E9.2.85.0"),sQuery(id+"F0.wireOp",EDGE,"E9.3.85.0"),sQuery(id+"F0.wireOp",EDGE,"E9.2.86.0"),sQuery(id+"F0.wireOp",EDGE,"E9.3.86.0"),sQuery(id+"F0.wireOp",EDGE,"E9.2.87.0"),sQuery(id+"F0.wireOp",EDGE,"E9.3.87.0"),sQuery(id+"F0.wireOp",EDGE,"E9.2.88.0"),sQuery(id+"F0.wireOp",EDGE,"E9.3.88.0"),sQuery(id+"F0.wireOp",EDGE,"E4"),sQuery(id+"F0.wireOp",EDGE,"E5")])]});
            var Q2;
            Q2=qCreatedBy(makeId("Top.planeOp"),FACE);
            mirror(context, id + "F5", {"entities" : qUnion([Q0, Q1]), "mirrorPlane" : qUnion([Q2])});
        }
    });
